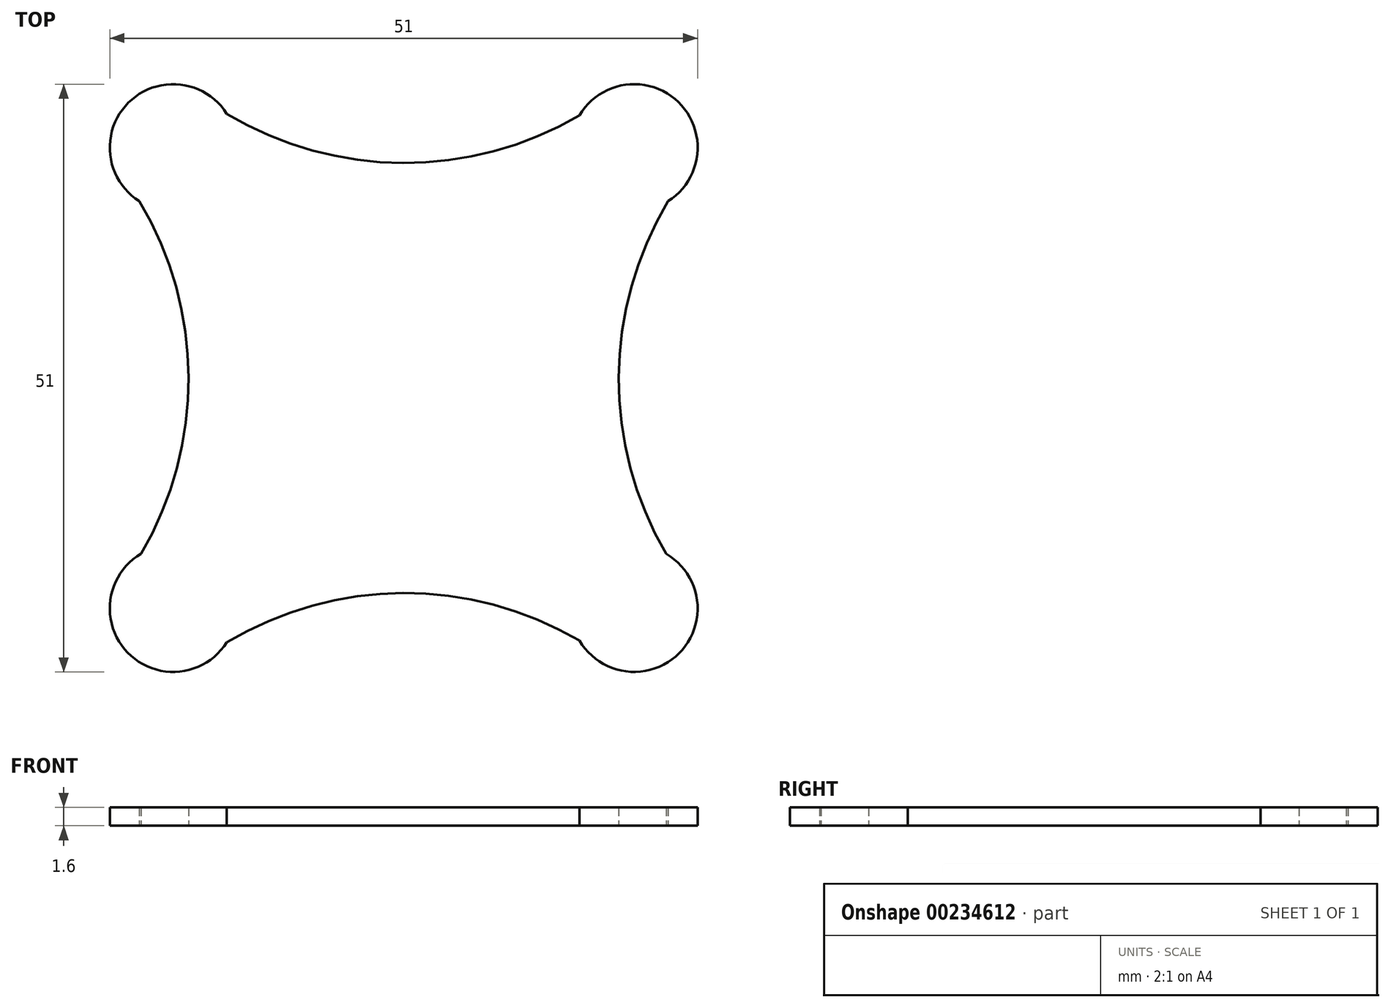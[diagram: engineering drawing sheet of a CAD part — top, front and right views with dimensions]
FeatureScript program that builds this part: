
annotation { "Feature Type Name" : "Feature", "Feature Type Description" : "" }
export const myFeature = defineFeature(function(context is Context, id is Id, definition is map)
    precondition{}
    {
        {
            var Q0;
            Q0=qCreatedBy(makeId("Top.planeOp"),FACE);
            var sketch = newSketch(context, id + "F0", { "sketchPlane" : qUnion([Q0])});
            skPoint(sketch, "E0.middle", {"position": v(0, 0) * mm});
            skArc(sketch, "E1", {"start": v(-22.78, -15.26) * mm, "mid": v(-18.66, 0.07) * mm, "end": v(-22.93, 15.35) * mm});
            skArc(sketch, "E2.MirrorCS", {"start": v(22.78, -15.26) * mm, "mid": v(18.66, 0.07) * mm, "end": v(22.93, 15.35) * mm});
            skArc(sketch, "E3.MirrorCS", {"start": v(15.26, -22.78) * mm, "mid": v(-0.07, -18.66) * mm, "end": v(-15.35, -22.93) * mm});
            skArc(sketch, "E4.MirrorCS", {"start": v(15.26, 22.78) * mm, "mid": v(-0.07, 18.66) * mm, "end": v(-15.35, 22.93) * mm});
            skPoint(sketch, "E5.orphan", {"position": v(24.2, 17.3) * mm});
            skArc(sketch, "E6", {"start": v(-15.35, 22.93) * mm, "mid": v(-23.89, 23.89) * mm, "end": v(-22.93, 15.35) * mm});
            skArc(sketch, "E7.MirrorC", {"start": v(15.26, 22.78) * mm, "mid": v(23.83, 23.95) * mm, "end": v(22.93, 15.35) * mm});
            skArc(sketch, "E8.MirrorC", {"start": v(-15.35, -22.93) * mm, "mid": v(-23.95, -23.83) * mm, "end": v(-22.78, -15.26) * mm});
            skArc(sketch, "E9.MirrorC", {"start": v(15.26, -22.78) * mm, "mid": v(23.89, -23.89) * mm, "end": v(22.78, -15.26) * mm});
            skPoint(sketch, "E10.orphan", {"position": v(-24.2, 17.3) * mm});
            skPoint(sketch, "E11.orphan", {"position": v(23.52, -16.45) * mm});
            skPoint(sketch, "E12.orphan", {"position": v(-23.52, -16.45) * mm});
            skSolve(sketch);
        }
        {
            var Q0;
            Q0 = qSketchRegion(id + "F0", true);
            extrude(context, id + "F1", {"entities" : qUnion([Q0]), "depth" : 1.6 * mm});
        }
    });
